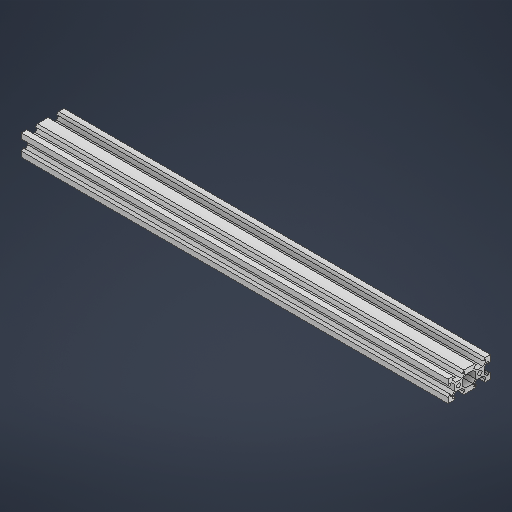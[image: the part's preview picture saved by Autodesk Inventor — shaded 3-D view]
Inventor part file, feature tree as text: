
AUTODESK INVENTOR PART (.ipt)
format: ipt  version: 2025.1 (Build 291241000, 241)  size: 317,440 bytes
history: native  units: mm
features: sketch x3, extrude x1
ambient origin geometry x8: Origin, YZ Plane, XZ Plane, XY Plane, X Axis, Y Axis, Z Axis, Center Point
bodies: Solid1 (feature_tree)
feature tree (4):
  extrude  "Extrusion1"  Depth=1.8mm
  sketch  "Sketch1"  dims[d1=40.0mm]
  sketch  "Sketch Circular Pattern1"  dims[d2=19.9mm d3=19.9mm d4=6.25mm d5=5.7mm d6=0.75mm d7=4.0mm d8=1.8mm d9=45.0deg d10=1.65mm d11=360.0deg d13=40.0mm]
  sketch  "Sketch Circular Pattern2"  dims[d14=19.9mm d15=19.9mm d16=6.25mm d17=5.7mm d18=0.75mm d19=4.0mm d20=1.8mm d21=45.0deg d22=1.65mm d23=360.0deg d24=400.0mm d25=0.0mm]
